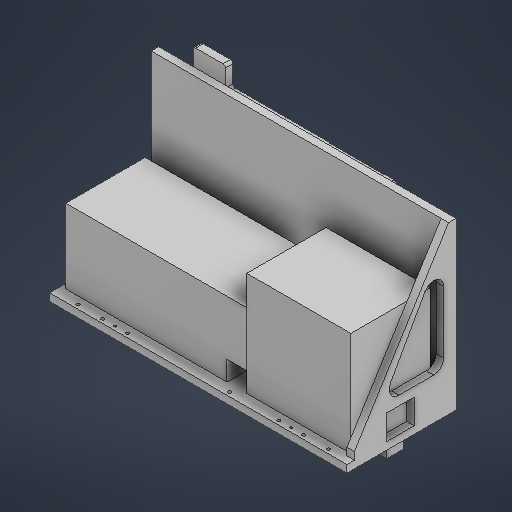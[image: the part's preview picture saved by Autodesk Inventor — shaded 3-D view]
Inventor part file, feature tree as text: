
AUTODESK INVENTOR PART (.ipt)
format: ipt  version: 2025 (Build 290162000, 162)  size: 304,640 bytes
history: native  units: in
note: dims shown in document units (in); Inventor stores cm internally (conversion verified against a paired STEP export)
features: hole x2, sketch x1
ambient origin geometry x8: Origin, YZ Plane, XZ Plane, XY Plane, X Axis, Y Axis, Z Axis, Center Point
bodies: Solid1 (feature_tree), Body1 (feature_tree)
feature tree (3):
  sketch  "Sketch1"  dims[d2=0.1969in d3=0.1969in d4=1.2008in d5=0.5906in d6=0.1969in d7=1.9685in d8=0.1969in d9=0.9843in d10=0.1969in d11=0.9843in d12=1.9488in d13=0.5906in d14=0.1969in d15=3.9173in d16=0.1969in d17=4.9016in d18=0.9843in d19=0.1969in d20=0.9843in d35=0.1936in d36=0.4724in d37=0.1575in d38=0.0787in d39=90.0deg d40=0.315in d41=0.0in d42=0.2559in d43=0.4724in d44=0.1575in d45=0.0787in d46=90.0deg d47=0.315in d48=0.0in d49=0.1969in d50=3.937in d21=0.0394in d22=0.0394in d23=0.0394in d24=0.0059in d25=0.0098in d26=0.0148in d27=32.2835in d28=0.0295in d29=46.4567in d30=0.0025in d31=0.0295in d32=0.0148in d33=0.0148in d34=32.2835in]
  hole  "Hole3"  [1 undecoded]
  hole  "Hole4"  [1 undecoded]
note: 2 required parameter values undecoded (feature->parameter linkage not recoverable at this tier; creation-order binding heuristic only, values carry confidence <= 0.55)
